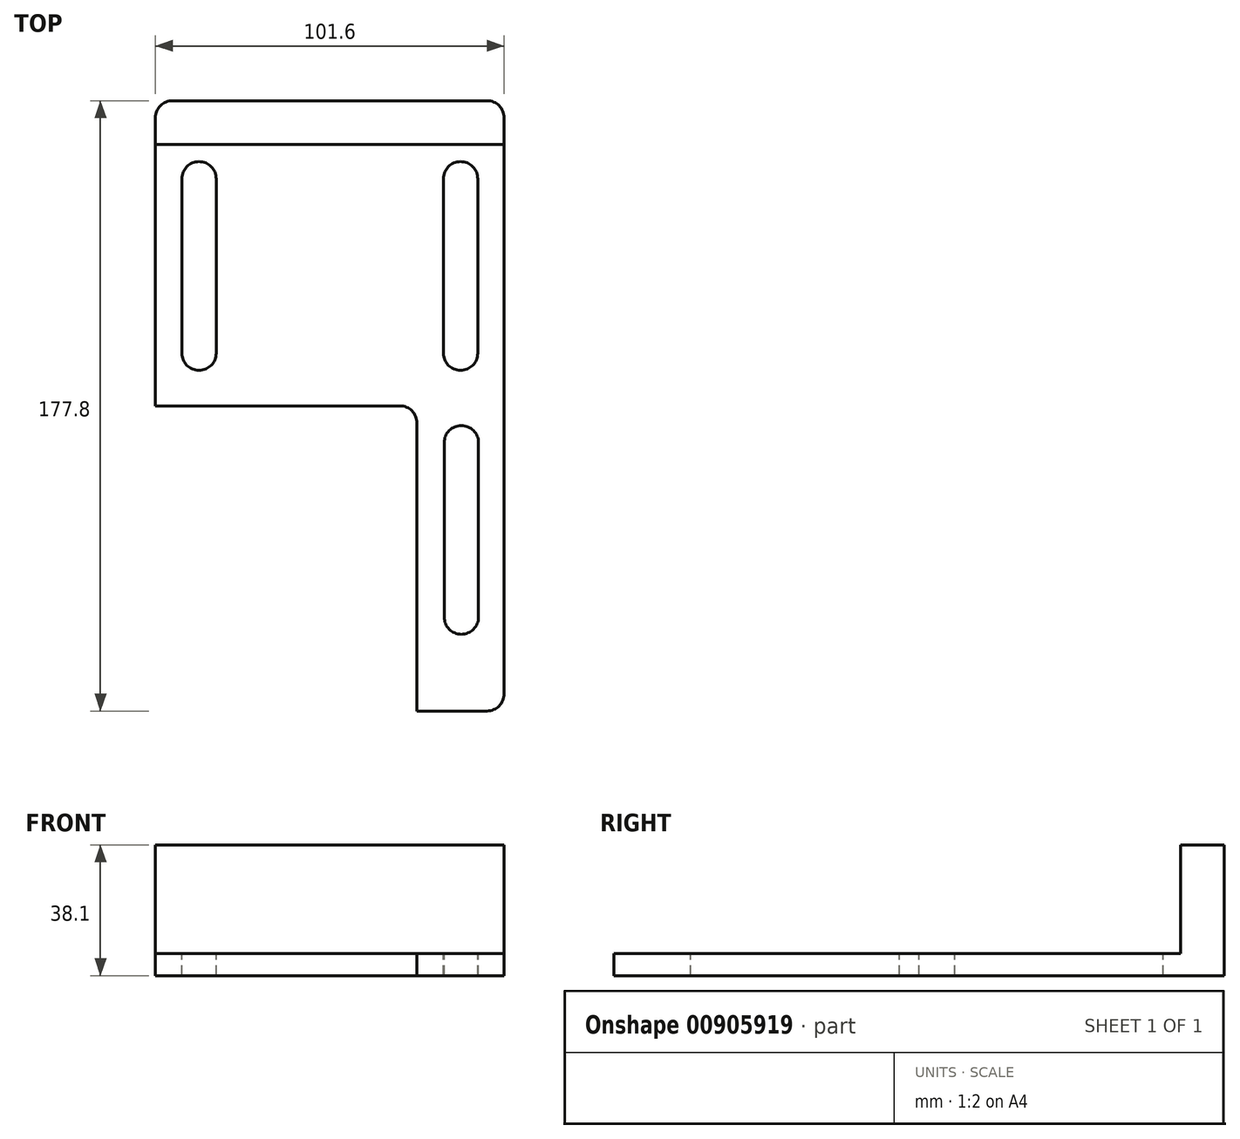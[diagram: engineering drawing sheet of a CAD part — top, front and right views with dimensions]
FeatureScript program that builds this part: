
annotation { "Feature Type Name" : "Feature", "Feature Type Description" : "" }
export const myFeature = defineFeature(function(context is Context, id is Id, definition is map)
    precondition{}
    {
        {
            var Q0;
            Q0=qCreatedBy(makeId("Top.planeOp"),FACE);
            var sketch = newSketch(context, id + "F0", { "sketchPlane" : qUnion([Q0])});
            skLineSegment(sketch, "E0.bottom", {"start": v(50.8, -88.9) * mm, "end": v(-50.8, -88.9) * mm});
            skLineSegment(sketch, "E0.top", {"start": v(50.8, 88.9) * mm, "end": v(-50.8, 88.9) * mm});
            skLineSegment(sketch, "E0.left", {"start": v(50.8, -88.9) * mm, "end": v(50.8, 88.9) * mm});
            skLineSegment(sketch, "E0.right", {"start": v(-50.8, -88.9) * mm, "end": v(-50.8, 88.9) * mm});
            skLineSegment(sketch, "E1.top", {"start": v(50.8, 76.2) * mm, "end": v(-50.8, 76.2) * mm});
            skLineSegment(sketch, "E1.left", {"start": v(50.8, 88.9) * mm, "end": v(50.8, 76.2) * mm});
            skLineSegment(sketch, "E1.right", {"start": v(-50.8, 88.9) * mm, "end": v(-50.8, 76.2) * mm});
            skLineSegment(sketch, "E2", {"start": v(-33.1, -10.1) * mm, "end": v(-33.1, -60.87) * mm});
            skLineSegment(sketch, "E3", {"start": v(-43.1, -10.07) * mm, "end": v(-43.1, -60.87) * mm});
            skArc(sketch, "E4", {"start": v(-43.1, -10.07) * mm, "mid": v(-38.08, -5.07) * mm, "end": v(-33.1, -10.1) * mm});
            skArc(sketch, "E5", {"start": v(-43.1, -60.87) * mm, "mid": v(-38.1, -65.87) * mm, "end": v(-33.1, -60.87) * mm});
            skLineSegment(sketch, "E6.bottom", {"start": v(-33.1, 15.33) * mm, "end": v(-43.1, 15.33) * mm});
            skLineSegment(sketch, "E6.top", {"start": v(-33.1, 66.13) * mm, "end": v(-43.1, 66.13) * mm});
            skLineSegment(sketch, "E6.left", {"start": v(-33.1, 15.33) * mm, "end": v(-33.1, 66.13) * mm});
            skLineSegment(sketch, "E6.right", {"start": v(-43.1, 15.33) * mm, "end": v(-43.1, 66.13) * mm});
            skPoint(sketch, "E6.middle", {"position": v(-38.1, 40.73) * mm});
            skLineSegment(sketch, "E7.bottom", {"start": v(43.1, 15.33) * mm, "end": v(33.1, 15.33) * mm});
            skLineSegment(sketch, "E7.top", {"start": v(43.1, 66.13) * mm, "end": v(33.1, 66.13) * mm});
            skLineSegment(sketch, "E7.left", {"start": v(43.1, 15.33) * mm, "end": v(43.1, 66.13) * mm});
            skLineSegment(sketch, "E7.right", {"start": v(33.1, 15.33) * mm, "end": v(33.1, 66.13) * mm});
            skPoint(sketch, "E7.middle", {"position": v(38.1, 40.73) * mm});
            skCircle(sketch, "E8", {"center": v(-38.1, 66.13) * mm, "radius": 5 * mm});
            skCircle(sketch, "E9", {"center": v(-38.1, 15.33) * mm, "radius": 5 * mm});
            skCircle(sketch, "E10", {"center": v(38.1, 15.33) * mm, "radius": 5 * mm});
            skCircle(sketch, "E11", {"center": v(38.1, 66.13) * mm, "radius": 5 * mm});
            skLineSegment(sketch, "E12.bottom", {"start": v(33.33, -10.75) * mm, "end": v(43.33, -10.75) * mm});
            skLineSegment(sketch, "E12.top", {"start": v(33.33, -61.55) * mm, "end": v(43.33, -61.55) * mm});
            skLineSegment(sketch, "E12.left", {"start": v(33.33, -10.75) * mm, "end": v(33.33, -61.55) * mm});
            skLineSegment(sketch, "E12.right", {"start": v(43.33, -10.75) * mm, "end": v(43.33, -61.55) * mm});
            skPoint(sketch, "E12.middle", {"position": v(38.33, -36.15) * mm});
            skArc(sketch, "E13", {"start": v(43.33, -10.75) * mm, "mid": v(38.33, -5.75) * mm, "end": v(33.33, -10.75) * mm});
            skArc(sketch, "E14", {"start": v(33.33, -61.55) * mm, "mid": v(38.33, -66.55) * mm, "end": v(43.33, -61.55) * mm});
            skLineSegment(sketch, "E15", {"start": v(-43.1, -10.07) * mm, "end": v(-50.8, -10.07) * mm});
            skLineSegment(sketch, "E16", {"start": v(43.33, -10.75) * mm, "end": v(50.8, -10.75) * mm});
            skLineSegment(sketch, "E17", {"start": v(-50.8, -88.9) * mm, "end": v(-25.4, -88.9) * mm});
            skLineSegment(sketch, "E18", {"start": v(50.8, -88.9) * mm, "end": v(25.4, -88.9) * mm});
            skLineSegment(sketch, "E19", {"start": v(25.4, -88.9) * mm, "end": v(25.4, 0) * mm});
            skLineSegment(sketch, "E20", {"start": v(25.4, 0) * mm, "end": v(-50.8, 0) * mm});
            skSolve(sketch);
        }
        {
            var Q0;
            Q0=qSketchRegion(id+"F0",true);
            extrude(context, id + "F1", {"entities" : qUnion([Q0]), "depth" : -6.4 * mm, "offsetDistance" : 25 * mm});
        }
        {
            var Q0;
            Q0=makeQuery(id+"F0.imprint","IMPRINT",FACE,{"disambiguationData":[TD([[makeQuery(id+"F0.imprint","IMPRINT",EDGE,{"derivedFrom":sQuery(id+"F0.wireOp",EDGE,"E0.top")}),1.0]])]});
            extrude(context, id + "F2", {"entities" : qUnion([Q0]), "operationType" : NewBodyOperationType.ADD, "depth" : 31.7 * mm, "offsetDistance" : 25 * mm});
        }
        {
            var Q0;
            {var subQ3=sQuery(id+"F0.wireOp",EDGE,"E0.bottom");Q0=makeQuery(id+"F0.imprint","IMPRINT",FACE,{"disambiguationData":[TD([[makeQuery(id+"F0.imprint","IMPRINT",EDGE,{"derivedFrom":subQ3}),-1.0]])]});}
            extrude(context, id + "F3", {"entities" : qUnion([Q0]), "operationType" : NewBodyOperationType.REMOVE, "oppositeDirection" : true, "depth" : 6.4 * mm, "offsetDistance" : 25 * mm});
        }
        {
            var Q0;
            Q0=makeQuery(id+"F2.opExtrude","CAP_EDGE",EDGE,{"disambiguationData":[OSD([sQuery(id+"F0.wireOp",EDGE,"E1.top")])],"isStart":true});
            var Q1;
            {var subQ0=sQuery(id+"F0.wireOp",EDGE,"E1.left");var subQ1=sQuery(id+"F0.wireOp",EDGE,"E0.top");Q1=makeQuery(id+"F2.boolean.opBoolean","MERGE",EDGE,{"derivedFrom":[makeQuery(id+"F1.opExtrude","SWEPT_EDGE",EDGE,{"disambiguationData":[OSD([subQ1,subQ0])]}),makeQuery(id+"F2.opExtrude","SWEPT_EDGE",EDGE,{"disambiguationData":[OSD([subQ1,subQ0])]})]});}
            var Q2;
            {var subQ0=sQuery(id+"F0.wireOp",EDGE,"E1.right");var subQ1=sQuery(id+"F0.wireOp",EDGE,"E0.top");Q2=makeQuery(id+"F2.boolean.opBoolean","MERGE",EDGE,{"derivedFrom":[makeQuery(id+"F1.opExtrude","SWEPT_EDGE",EDGE,{"disambiguationData":[OSD([subQ1,subQ0])]}),makeQuery(id+"F2.opExtrude","SWEPT_EDGE",EDGE,{"disambiguationData":[OSD([subQ1,subQ0])]})]});}
            var Q3;
            Q3=makeQuery(id+"F1.opExtrude","SWEPT_EDGE",EDGE,{"disambiguationData":[OSD([sQuery(id+"F0.wireOp",EDGE,"E0.right"),sQuery(id+"F0.wireOp",EDGE,"E17")])]});
            var Q4;
            Q4=makeQuery(id+"F1.opExtrude","SWEPT_EDGE",EDGE,{"disambiguationData":[OSD([sQuery(id+"F0.wireOp",EDGE,"E0.left"),sQuery(id+"F0.wireOp",EDGE,"E18")])]});
            var Q5;
            Q5=makeQuery(id+"F3.boolean.opBoolean","COPY",EDGE,{"derivedFrom":makeQuery(id+"F3.opExtrude","SWEPT_EDGE",EDGE,{"disambiguationData":[OSD([sQuery(id+"F0.wireOp",EDGE,"E19"),sQuery(id+"F0.wireOp",EDGE,"E20")])]})});
            var Q6;
            Q6=makeQuery(id+"F3.boolean.opBoolean","COPY",EDGE,{"derivedFrom":makeQuery(id+"F3.opExtrude","SWEPT_EDGE",EDGE,{"disambiguationData":[OSD([sQuery(id+"F0.wireOp",EDGE,"E0.right"),sQuery(id+"F0.wireOp",EDGE,"E20")])]})});
            var Q7;
            Q7=makeQuery(id+"F3.boolean.opBoolean","COPY",EDGE,{"derivedFrom":makeQuery(id+"F3.opExtrude","SWEPT_EDGE",EDGE,{"disambiguationData":[OSD([sQuery(id+"F0.wireOp",EDGE,"E0.bottom"),sQuery(id+"F0.wireOp",EDGE,"E18"),sQuery(id+"F0.wireOp",EDGE,"E19")])]})});
            fillet(context, id + "F4", {"entities" : qUnion([Q0, Q1, Q2, Q3, Q4, Q5, Q6, Q7]), "radius" : 5 * mm, "tangentPropagation" : true, "allowEdgeOverflow" : false});
        }
    });
